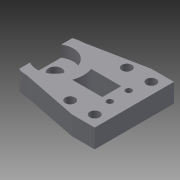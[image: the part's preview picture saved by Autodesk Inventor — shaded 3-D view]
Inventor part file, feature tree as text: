
AUTODESK INVENTOR PART (.ipt)
format: ipt  version: 2015 (Build 190159000, 159)  size: 184,320 bytes
history: native  units: in
note: dims shown in document units (in); Inventor stores cm internally (conversion verified against a paired STEP export)
features: extrude x5, sketch x2
ambient origin geometry x8: Origin, YZ Plane, XZ Plane, XY Plane, X Axis, Y Axis, Z Axis, Center Point
bodies: Solid1 (feature_tree)
feature tree (7):
  extrude  "Extrusion1"  Depth=0.4724in
  sketch  "Sketch2"  dims[d2=0.1969in d3=0.1969in d4=0.1181in d5=0.1181in d6=0.1181in d7=0.1181in d8=0.1575in d9=0.126in d10=0.126in d11=0.5906in d12=0.0in d13=1.1811in d14=0.2756in d16=1.1811in d17=0.1969in d18=0.3937in d19=0.0in d30=0.2165in d31=0.2165in d32=0.3937in d33=0.1969in d36=0.7598in d37=0.2362in d38=0.0in d39=0.3937in d40=0.5118in d41=0.3937in d42=0.9843in d48=0.3937in d49=0.5118in d50=0.3937in d51=0.9843in d52=0.1969in d53=0.2362in d54=0.2362in d55=0.1969in d56=0.2362in d57=0.2047in d58=0.1969in d59=0.2362in d60=0.2047in d61=0.2047in d62=0.2047in d63=1.5748in d64=0.0in d65=1.5748in d66=0.0in]
  extrude  "Extrusion2"  Depth=0.2362in
  extrude  "Extrusion6"  Depth=0.2362in
  extrude  "Extrusion7"  Depth=0.2362in
  extrude  "Extrusion8"  Depth=0.2362in
  sketch  "Sketch1"  dims[d0=1.6535in d1=0.4724in]
